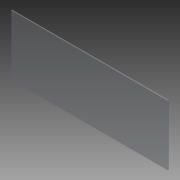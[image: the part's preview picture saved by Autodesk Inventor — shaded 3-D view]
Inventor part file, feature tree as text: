
AUTODESK INVENTOR PART (.ipt)
format: ipt  version: 2014 (Build 180170000, 170)  size: 69,632 bytes
history: native  units: in
note: dims shown in document units (in); Inventor stores cm internally (conversion verified against a paired STEP export)
features: extrude x1, sketch x1
ambient origin geometry x8: Origin, YZ Plane, XZ Plane, XY Plane, X Axis, Y Axis, Z Axis, Center Point
bodies: Solid1 (feature_tree)
feature tree (2):
  extrude  "Extrusion1"  Depth=8.0in
  sketch  "Sketch1"  dims[d0=20.8in d1=8.0in d2=0.125in d3=0.0in]
